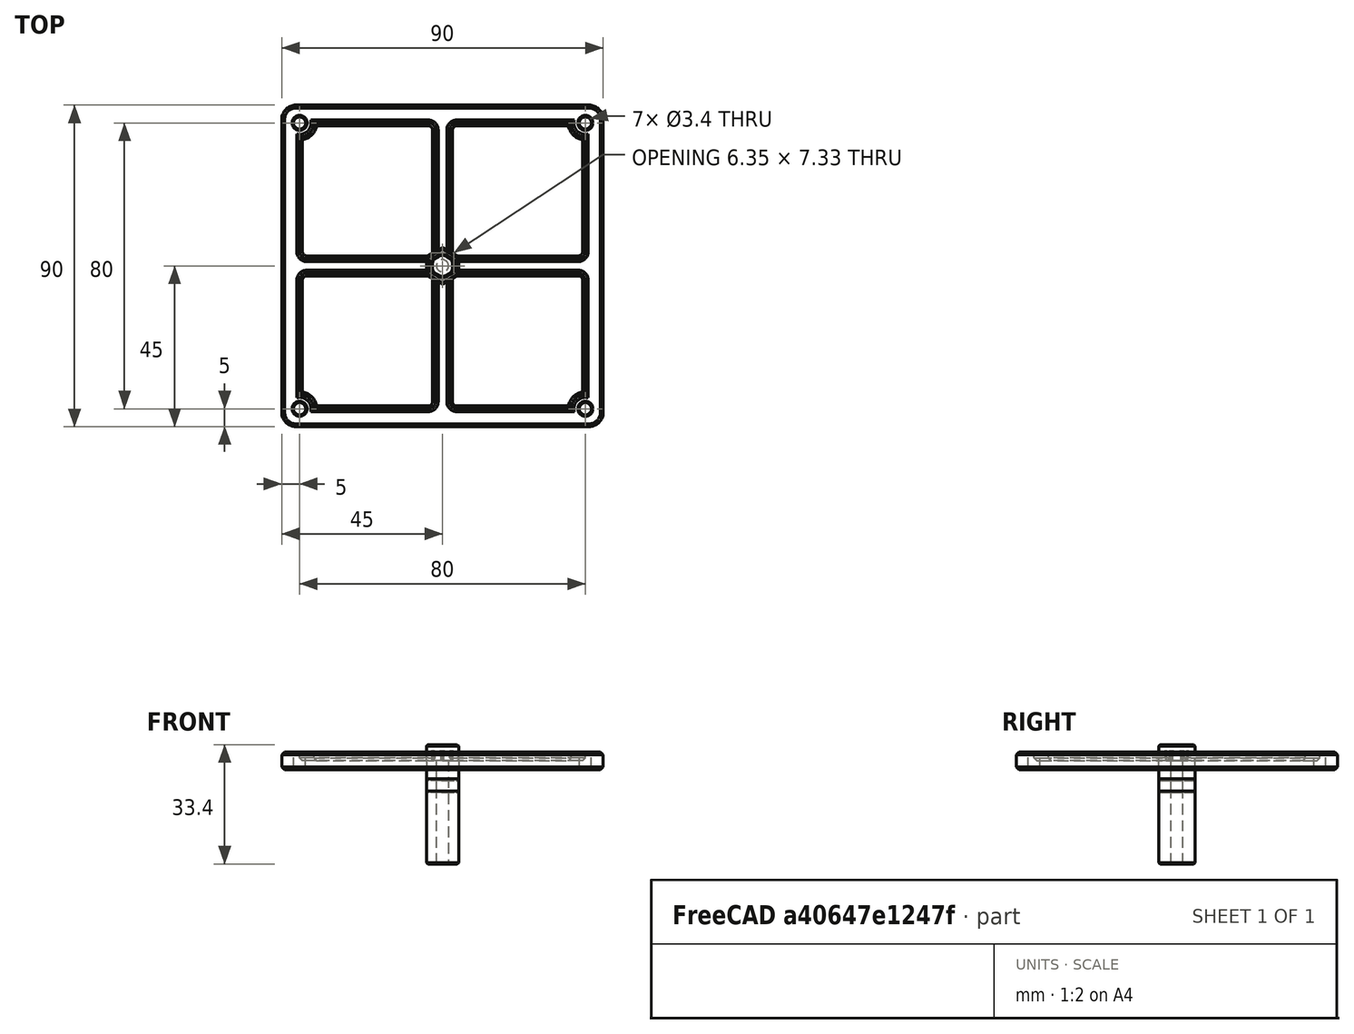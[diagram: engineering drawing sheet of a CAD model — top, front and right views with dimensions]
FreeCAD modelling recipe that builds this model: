
FCSTD DOCUMENT  (FreeCAD 1.1R20260325 (Git shallow))
Label: test_jig
License: All rights reserved
LicenseURL: http://en.wikipedia.org/wiki/All_rights_reserved
objects: Sketcher::SketchObject×9, PartDesign::Chamfer×8, PartDesign::Body×5, App::Point×5, PartDesign::Pad×4, PartDesign::Pocket×3, PartDesign::FeatureBase×3, PartDesign::Fillet×1, PartDesign::AdditiveLoft×1
note: 80 computed .brp shape members not serialized (recipe doc carries the construction recipe); baked Part::Feature solids carry a one-line shape summary decoded from their .brp

FEATURE [Sketcher::SketchObject] Sketch  label="dc_base_s"
  ArcFitTolerance = 1e-06
  AttachmentSupport = -> [XY_Plane]
  ExternalTypes = [0]
  FullyConstrained = true
  MakeInternals = false
  MapMode = 5
  _ExternalGeoVersion = 0
  sketch-geometry (4):
    g0: LineSegment StartX=-45 StartY=45 StartZ=0 EndX=-45 EndY=-45 EndZ=0
    g1: LineSegment StartX=-45 StartY=-45 StartZ=0 EndX=45 EndY=-45 EndZ=0
    g2: LineSegment StartX=45 StartY=-45 StartZ=0 EndX=45 EndY=45 EndZ=0
    g3: LineSegment StartX=45 StartY=45 StartZ=0 EndX=-45 EndY=45 EndZ=0
  constraints (10):
    c: Coincident(g0,g1)
    c: Coincident(g1,g2)
    c: Coincident(g2,g3)
    c: Coincident(g3,g0)
    c: Vertical(g2)
    c: Horizontal(g1)
    c: Symmetric(g0,g0,g-1)
    c: Symmetric(g0,g2,g-2)
    c: DistanceX(g1,g1) = 90  'dim2'
    c: DistanceY(g0,g0) = 90  'dim1'
FEATURE [PartDesign::Pad] Pad  label="dc_base"
  Direction = (0,0,1)
  Length = 5
  Length2 = 10
  Profile = -> Sketch
  ReferenceAxis = -> Sketch [N_Axis]
  Refine = true
  SideType = 2
  Suppressed = false
  Type = 0
  Type2 = 0
FEATURE [Sketcher::SketchObject] Sketch001  label="dc_grid_cut_s"
  ArcFitTolerance = 1e-06
  AttachmentSupport = -> [XY_Plane]
  ExternalTypes = [0]
  FullyConstrained = false
  MakeInternals = false
  MapMode = 5
  _ExternalGeoVersion = 0
  expr: .Constraints.corner_flt = <<dc_base_corner>>.Radius
  expr: .Constraints.dim1 = <<dc_base_s>>.Constraints.dim1
  expr: .Constraints.dim2 = <<dc_base_s>>.Constraints.dim2
  sketch-geometry (76):
    g0: LineSegment StartX=-40 StartY=36 StartZ=0 EndX=-40 EndY=4 EndZ=0
    g1: LineSegment StartX=-38 StartY=2 StartZ=0 EndX=-4 EndY=2 EndZ=0
    g2: LineSegment StartX=-2 StartY=4 StartZ=0 EndX=-2 EndY=38 EndZ=0
    g3: LineSegment StartX=-4 StartY=40 StartZ=0 EndX=-36 EndY=40 EndZ=0
    g4: LineSegment StartX=2 StartY=38 StartZ=0 EndX=2 EndY=4 EndZ=0
    g5: LineSegment StartX=4 StartY=2 StartZ=0 EndX=38 EndY=2 EndZ=0
    g6: LineSegment StartX=40 StartY=4 StartZ=0 EndX=40 EndY=36 EndZ=0
    g7: LineSegment StartX=36 StartY=40 StartZ=0 EndX=4 EndY=40 EndZ=0
    g8: LineSegment StartX=-40 StartY=-4 StartZ=0 EndX=-40 EndY=-36 EndZ=0
    g9: LineSegment StartX=-2 StartY=-38 StartZ=0 EndX=-2 EndY=-4 EndZ=0
    g10: LineSegment StartX=-4 StartY=-2 StartZ=0 EndX=-38 EndY=-2 EndZ=0
    g11: LineSegment StartX=2 StartY=-4 StartZ=0 EndX=2 EndY=-38 EndZ=0
    g12: LineSegment StartX=4 StartY=-40 StartZ=0 EndX=36 EndY=-40 EndZ=0
    g13: LineSegment StartX=40 StartY=-36 StartZ=0 EndX=40 EndY=-4 EndZ=0
    g14: LineSegment StartX=38 StartY=-2 StartZ=0 EndX=4 EndY=-2 EndZ=0
    g15: LineSegment [constr] StartX=-45 StartY=45 StartZ=0 EndX=-45 EndY=-45 EndZ=0
    g16: LineSegment [constr] StartX=-45 StartY=-45 StartZ=0 EndX=45 EndY=-45 EndZ=0
    g17: LineSegment [constr] StartX=45 StartY=-45 StartZ=0 EndX=45 EndY=45 EndZ=0
    g18: LineSegment [constr] StartX=45 StartY=45 StartZ=0 EndX=-45 EndY=45 EndZ=0
    g19: GeomPoint [constr] X=-40 Y=40 Z=0
    g20: ArcOfCircle CenterX=-4 CenterY=38 CenterZ=0 NormalX=0 NormalY=0 NormalZ=1 AngleXU=0 Radius=2 StartAngle=1.6e-15 EndAngle=1.5708
    g21: GeomPoint [constr] X=-2 Y=40 Z=0
    g22: ArcOfCircle CenterX=-4 CenterY=4 CenterZ=0 NormalX=0 NormalY=0 NormalZ=1 AngleXU=0 Radius=2 StartAngle=4.71239 EndAngle=6.28319
    g23: GeomPoint [constr] X=-2 Y=2 Z=0
    g24: ArcOfCircle CenterX=-38 CenterY=4 CenterZ=0 NormalX=0 NormalY=0 NormalZ=1 AngleXU=0 Radius=2 StartAngle=3.14159 EndAngle=4.71239
    g25: GeomPoint [constr] X=-40 Y=2 Z=0
    g26: ArcOfCircle CenterX=-38 CenterY=-4 CenterZ=0 NormalX=0 NormalY=0 NormalZ=1 AngleXU=0 Radius=2 StartAngle=1.5708 EndAngle=3.14159
    g27: GeomPoint [constr] X=-40 Y=-2 Z=0
    g28: GeomPoint [constr] X=-35 Y=-35 Z=0
    g29: ArcOfCircle CenterX=-4 CenterY=-38 CenterZ=0 NormalX=0 NormalY=0 NormalZ=1 AngleXU=0 Radius=2 StartAngle=4.71239 EndAngle=6.28319
    g30: GeomPoint [constr] X=-2 Y=-35 Z=0
    g31: ArcOfCircle CenterX=-4 CenterY=-4 CenterZ=0 NormalX=0 NormalY=0 NormalZ=1 AngleXU=0 Radius=2 StartAngle=1e-16 EndAngle=1.5708
    g32: GeomPoint [constr] X=-2 Y=-2 Z=0
    g33: ArcOfCircle CenterX=4 CenterY=38 CenterZ=0 NormalX=0 NormalY=0 NormalZ=1 AngleXU=0 Radius=2 StartAngle=1.5708 EndAngle=3.14159
    g34: GeomPoint [constr] X=2 Y=40 Z=0
    g35: GeomPoint [constr] X=40 Y=40 Z=0
    g36: ArcOfCircle CenterX=38 CenterY=-4 CenterZ=0 NormalX=0 NormalY=0 NormalZ=1 AngleXU=0 Radius=2 StartAngle=0 EndAngle=1.5708
    g37: GeomPoint [constr] X=40 Y=-2 Z=0
    g38: ArcOfCircle CenterX=4 CenterY=-4 CenterZ=0 NormalX=0 NormalY=0 NormalZ=1 AngleXU=0 Radius=2 StartAngle=1.5708 EndAngle=3.14159
    g39: GeomPoint [constr] X=2 Y=-2 Z=0
    g40: ArcOfCircle CenterX=4 CenterY=-38 CenterZ=0 NormalX=0 NormalY=0 NormalZ=1 AngleXU=0 Radius=2 StartAngle=3.14159 EndAngle=4.71239
    g41: GeomPoint [constr] X=2 Y=-40 Z=0
    g42: GeomPoint [constr] X=40 Y=-40 Z=0
    g43: ArcOfCircle CenterX=4 CenterY=4 CenterZ=0 NormalX=0 NormalY=0 NormalZ=1 AngleXU=0 Radius=2 StartAngle=3.14159 EndAngle=4.71239
    g44: GeomPoint [constr] X=2 Y=2 Z=0
    g45: ArcOfCircle CenterX=38 CenterY=4 CenterZ=0 NormalX=0 NormalY=0 NormalZ=1 AngleXU=0 Radius=2 StartAngle=4.71239 EndAngle=6.28319
    g46: GeomPoint [constr] X=40 Y=2 Z=0
    g47: LineSegment [constr] StartX=-4 StartY=2 StartZ=0 EndX=-4 EndY=-2 EndZ=0
    g48: LineSegment [constr] StartX=4 StartY=2 StartZ=0 EndX=4 EndY=-2 EndZ=0
    g49: LineSegment [constr] StartX=-2 StartY=4 StartZ=0 EndX=2 EndY=4 EndZ=0
    g50: LineSegment [constr] StartX=-2 StartY=-4 StartZ=0 EndX=2 EndY=-4 EndZ=0
    g51: Circle [constr] CenterX=0 CenterY=0 CenterZ=0 NormalX=0 NormalY=0 NormalZ=1 AngleXU=0 Radius=4
    g52: LineSegment [constr] StartX=-40 StartY=4 StartZ=0 EndX=-45 EndY=4 EndZ=0
    g53: LineSegment [constr] StartX=-40 StartY=-4 StartZ=0 EndX=-45 EndY=-4 EndZ=0
    g54: LineSegment [constr] StartX=40 StartY=4 StartZ=0 EndX=45 EndY=4 EndZ=0
    g55: LineSegment [constr] StartX=40 StartY=-4 StartZ=0 EndX=45 EndY=-4 EndZ=0
    g56: LineSegment [constr] StartX=4 StartY=-40 StartZ=0 EndX=4 EndY=-45 EndZ=0
    g57: LineSegment [constr] StartX=-4 StartY=-40 StartZ=0 EndX=-4 EndY=-45 EndZ=0
    g58: LineSegment [constr] StartX=-4 StartY=40 StartZ=0 EndX=-4 EndY=45 EndZ=0
    g59: LineSegment [constr] StartX=4 StartY=40 StartZ=0 EndX=4 EndY=45 EndZ=0
    g60: LineSegment [constr] StartX=-45 StartY=-40 StartZ=0 EndX=-40 EndY=-40 EndZ=0
    g61: LineSegment [constr] StartX=-40 StartY=-40 StartZ=0 EndX=-40 EndY=-45 EndZ=0
    g62: Circle [constr] CenterX=-40 CenterY=-40 CenterZ=0 NormalX=0 NormalY=0 NormalZ=1 AngleXU=0 Radius=1.7
    g63: Circle [constr] CenterX=-40 CenterY=-40 CenterZ=0 NormalX=0 NormalY=0 NormalZ=1 AngleXU=0 Radius=2.8
    g64: ArcOfCircle CenterX=-40 CenterY=-40 CenterZ=0 NormalX=0 NormalY=0 NormalZ=1 AngleXU=0 Radius=4 StartAngle=-9e-16 EndAngle=1.5708
    g65: ArcOfCircle [constr] CenterX=-41 CenterY=-41 CenterZ=0 NormalX=0 NormalY=0 NormalZ=1 AngleXU=0 Radius=4 StartAngle=3.14159 EndAngle=4.71239
    g66: LineSegment [constr] StartX=40 StartY=-45 StartZ=0 EndX=40 EndY=-40 EndZ=0
    g67: LineSegment [constr] StartX=40 StartY=-40 StartZ=0 EndX=45 EndY=-40 EndZ=0
    g68: LineSegment [constr] StartX=40 StartY=45 StartZ=0 EndX=40 EndY=40 EndZ=0
    g69: LineSegment [constr] StartX=40 StartY=40 StartZ=0 EndX=45 EndY=40 EndZ=0
    g70: LineSegment [constr] StartX=-45 StartY=40 StartZ=0 EndX=-40 EndY=40 EndZ=0
    g71: LineSegment [constr] StartX=-40 StartY=40 StartZ=0 EndX=-40 EndY=45 EndZ=0
    g72: ArcOfCircle CenterX=40 CenterY=-40 CenterZ=0 NormalX=0 NormalY=0 NormalZ=1 AngleXU=0 Radius=4 StartAngle=1.5708 EndAngle=3.14159
    g73: ArcOfCircle CenterX=40 CenterY=40 CenterZ=0 NormalX=0 NormalY=0 NormalZ=1 AngleXU=0 Radius=4 StartAngle=3.14159 EndAngle=4.71239
    g74: ArcOfCircle CenterX=-40 CenterY=40 CenterZ=0 NormalX=0 NormalY=0 NormalZ=1 AngleXU=0 Radius=4 StartAngle=4.71239 EndAngle=6.28319
    g75: LineSegment StartX=-36 StartY=-40 StartZ=0 EndX=-4 EndY=-40 EndZ=0
  constraints (192):
    c: Vertical(g0)
    c: Vertical(g2)
    c: Horizontal(g1)
    c: Horizontal(g3)
    c: Vertical(g4)
    c: Vertical(g6)
    c: Horizontal(g5)
    c: Horizontal(g7)
    c: Vertical(g8)
    c: Vertical(g9)
    c: Horizontal(g10)
    c: Vertical(g11)
    c: Vertical(g13)
    c: Horizontal(g12)
    c: Horizontal(g14)
    c: Coincident(g15,g16)
    c: Coincident(g16,g17)
    c: Coincident(g17,g18)
    c: Coincident(g18,g15)
    c: Vertical(g17)
    c: Horizontal(g16)
    c: Symmetric(g15,g17,g-2)
    c: Symmetric(g15,g15,g-1)
    c: DistanceX(g16,g16) = 90  'dim2'
    c: DistanceY(g15,g15) = 90  'dim1'
    c: PointOnObject(g19,g0)
    c: PointOnObject(g19,g3)
    c: PointOnObject(g21,g3)
    c: PointOnObject(g21,g2)
    c: Tangent(g3,g20) = -1.5708
    c: Tangent(g2,g20) = -1.5708
    c: PointOnObject(g23,g2)
    c: PointOnObject(g23,g1)
    c: Tangent(g2,g22) = -1.5708
    c: Tangent(g1,g22) = -1.5708
    c: PointOnObject(g25,g1)
    c: PointOnObject(g25,g0)
    c: Tangent(g1,g24) = -1.5708
    c: Tangent(g0,g24) = -1.5708
    c: PointOnObject(g27,g10)
    c: PointOnObject(g27,g8)
    c: Tangent(g10,g26) = -1.5708
    c: Tangent(g8,g26) = -1.5708
    c: PointOnObject(g30,g9)
    c: Tangent(g9,g29) = -1.5708
    c: PointOnObject(g32,g10)
    c: PointOnObject(g32,g9)
    c: Tangent(g10,g31) = -1.5708
    c: Tangent(g9,g31) = -1.5708
    c: PointOnObject(g34,g7)
    c: PointOnObject(g34,g4)
    c: Tangent(g7,g33) = -1.5708
    c: Tangent(g4,g33) = -1.5708
    c: PointOnObject(g35,g7)
    c: PointOnObject(g35,g6)
    c: PointOnObject(g37,g14)
    c: PointOnObject(g37,g13)
    c: Tangent(g14,g36) = -1.5708
    c: Tangent(g13,g36) = -1.5708
    c: PointOnObject(g39,g14)
    c: PointOnObject(g39,g11)
    c: Tangent(g14,g38) = -1.5708
    c: Tangent(g11,g38) = -1.5708
    c: PointOnObject(g41,g11)
    c: PointOnObject(g41,g12)
    c: Tangent(g11,g40) = -1.5708
    c: Tangent(g12,g40) = -1.5708
    c: PointOnObject(g42,g12)
    c: PointOnObject(g42,g13)
    c: PointOnObject(g44,g4)
    c: PointOnObject(g44,g5)
    c: Tangent(g4,g43) = -1.5708
    c: Tangent(g5,g43) = -1.5708
    c: PointOnObject(g46,g5)
    c: PointOnObject(g46,g6)
    c: Tangent(g5,g45) = -1.5708
    c: Tangent(g6,g45) = -1.5708
    c: Coincident(g47,g1)
    c: Coincident(g47,g10)
    c: Vertical(g47)
    c: Coincident(g48,g5)
    c: Coincident(g48,g14)
    c: Coincident(g49,g2)
    c: Coincident(g49,g4)
    c: Coincident(g50,g9)
    c: Coincident(g50,g11)
    c: Horizontal(g49)
    c: Horizontal(g50)
    c: Vertical(g48)
    c: DistanceY(g47,g47) = 4  'rim_inner'
    c: Coincident(g51,g-1)
    c: Tangent(g49,g51)
    c: Tangent(g48,g51)
    c: Tangent(g50,g51)
    c: Tangent(g51,g47)
    c: Coincident(g52,g0)
    c: PointOnObject(g52,g15)
    c: Horizontal(g52)
    c: Coincident(g53,g8)
    c: PointOnObject(g53,g15)
    c: Horizontal(g53)
    c: Coincident(g54,g6)
    c: PointOnObject(g54,g17)
    c: Coincident(g55,g13)
    c: PointOnObject(g55,g17)
    c: Coincident(g56,g12)
    c: PointOnObject(g56,g16)
    c: PointOnObject(g57,g16)
    c: Coincident(g58,g3)
    c: PointOnObject(g58,g18)
    c: Coincident(g59,g7)
    c: PointOnObject(g59,g18)
    c: Vertical(g57)
    c: Vertical(g56)
    c: Vertical(g58)
    c: Vertical(g59)
    c: Horizontal(g54)
    c: Horizontal(g55)
    c: Equal(g52,g53)
    c: Equal(g53,g57)
    c: Equal(g57,g56)
    c: Equal(g56,g55)
    c: Equal(g55,g54)
    c: Equal(g54,g59)
    c: Equal(g59,g58)
    c: Distance(g52,g52) = 5  'rib_outer'
    c: PointOnObject(g60,g15)
    c: Horizontal(g60)
    c: Coincident(g60,g61)
    c: PointOnObject(g61,g16)
    c: Vertical(g61)
    c: Coincident(g62,g60)
    c: Coincident(g63,g60)
    c: Diameter(g62) = 3.4  'screw_hole'
    c: Diameter(g63) = 5.6  'screw_head'
    c: Coincident(g64,g60)
    c: DistanceX(g60,g60) = 5  'screw_inset'
    c: Equal(g61,g60)
    c: Tangent(g65,g15) = -1.5708
    c: Tangent(g65,g16) = -1.5708
    c: Radius(g65) = 4  'corner_flt'
    c: PointOnObject(g66,g16)
    c: Vertical(g66)
    c: Coincident(g66,g67)
    c: PointOnObject(g67,g17)
    c: Horizontal(g67)
    c: PointOnObject(g68,g18)
    c: Vertical(g68)
    c: Coincident(g68,g69)
    c: PointOnObject(g69,g17)
    c: Horizontal(g69)
    c: PointOnObject(g70,g15)
    c: Coincident(g70,g71)
    c: PointOnObject(g71,g18)
    c: Radius(g20) = 2  'corner_fillet'
    c: Horizontal(g70)
    c: Vertical(g71)
    c: Equal(g61,g66)
    c: Equal(g66,g67)
    c: Equal(g67,g69)
    c: Equal(g69,g68)
    c: Equal(g68,g71)
    c: Equal(g71,g70)
    c: Coincident(g72,g42)
    c: Coincident(g73,g35)
    c: Coincident(g74,g19)
    c: Coincident(g3,g74)
    c: Coincident(g0,g74)
    c: Coincident(g7,g73)
    c: Coincident(g6,g73)
    c: Coincident(g13,g72)
    c: Coincident(g12,g72)
    c: Coincident(g8,g64)
    c: Equal(g20,g33)
    c: Equal(g33,g45)
    c: Equal(g45,g36)
    c: Equal(g36,g40)
    c: Equal(g40,g29)
    c: Equal(g29,g26)
    c: Equal(g26,g24)
    c: Equal(g24,g43)
    c: Equal(g43,g38)
    c: Equal(g38,g31)
    c: Equal(g31,g22)
    c: Coincident(g75,g64)
    c: Horizontal(g75)
    c: Tangent(g29,g75) = -1.5708
    c: Coincident(g57,g29)
    c: Equal(g72,g64)
    c: Equal(g64,g74)
    c: Equal(g74,g73)
    c: Radius(g64) = 4  'screw_pad'
FEATURE [PartDesign::Fillet] Fillet  label="dc_base_corner"
  Base = -> Pad [Edge2,Edge5,Edge8,Edge1]
  BaseFeature = -> Pad
  Radius = 4
  Refine = true
  SupportTransform = false
  Suppressed = false
  UseAllEdges = false
FEATURE [PartDesign::Pocket] Pocket  label="dc_grid_cut"
  BaseFeature = -> Fillet
  Direction = (0,0,-1)
  Length = 5
  Length2 = 5
  Profile = -> Sketch001
  ReferenceAxis = -> Sketch001 [N_Axis]
  Refine = true
  Reversed = true
  SideType = 0
  Suppressed = false
  Type = 1
  Type2 = 0
FEATURE [Sketcher::SketchObject] Sketch002  label="dc_holes_s"
  ArcFitTolerance = 1e-06
  AttachmentSupport = -> [XY_Plane]
  ExternalTypes = [0]
  FullyConstrained = true
  MakeInternals = false
  MapMode = 5
  _ExternalGeoVersion = 0
  expr: .Constraints.dim1 = <<dc_base_s>>.Constraints.dim1
  expr: .Constraints.dim2 = <<dc_base_s>>.Constraints.dim2
  expr: .Constraints.head = <<dc_grid_cut_s>>.Constraints.screw_head
  expr: .Constraints.hole = <<dc_grid_cut_s>>.Constraints.screw_hole
  expr: .Constraints.inset = <<dc_grid_cut_s>>.Constraints.screw_inset
  sketch-geometry (17):
    g0: LineSegment [constr] StartX=-45 StartY=45 StartZ=0 EndX=-45 EndY=-45 EndZ=0
    g1: LineSegment [constr] StartX=-45 StartY=-45 StartZ=0 EndX=45 EndY=-45 EndZ=0
    g2: LineSegment [constr] StartX=45 StartY=-45 StartZ=0 EndX=45 EndY=45 EndZ=0
    g3: LineSegment [constr] StartX=45 StartY=45 StartZ=0 EndX=-45 EndY=45 EndZ=0
    g4: LineSegment [constr] StartX=-40 StartY=45 StartZ=0 EndX=-40 EndY=40 EndZ=0
    g5: LineSegment [constr] StartX=-40 StartY=40 StartZ=0 EndX=-45 EndY=40 EndZ=0
    g6: LineSegment [constr] StartX=40 StartY=45 StartZ=0 EndX=40 EndY=40 EndZ=0
    g7: LineSegment [constr] StartX=40 StartY=40 StartZ=0 EndX=45 EndY=40 EndZ=0
    g8: LineSegment [constr] StartX=-45 StartY=-40 StartZ=0 EndX=-40 EndY=-40 EndZ=0
    g9: LineSegment [constr] StartX=-40 StartY=-40 StartZ=0 EndX=-40 EndY=-45 EndZ=0
    g10: LineSegment [constr] StartX=45 StartY=-40 StartZ=0 EndX=40 EndY=-40 EndZ=0
    g11: LineSegment [constr] StartX=40 StartY=-40 StartZ=0 EndX=40 EndY=-45 EndZ=0
    g12: Circle CenterX=-40 CenterY=-40 CenterZ=0 NormalX=0 NormalY=0 NormalZ=1 AngleXU=0 Radius=1.7
    g13: Circle CenterX=40 CenterY=-40 CenterZ=0 NormalX=0 NormalY=0 NormalZ=1 AngleXU=0 Radius=1.7
    g14: Circle CenterX=40 CenterY=40 CenterZ=0 NormalX=0 NormalY=0 NormalZ=1 AngleXU=0 Radius=1.7
    g15: Circle CenterX=-40 CenterY=40 CenterZ=0 NormalX=0 NormalY=0 NormalZ=1 AngleXU=0 Radius=1.7
    g16: Circle [constr] CenterX=-40 CenterY=-40 CenterZ=0 NormalX=0 NormalY=0 NormalZ=1 AngleXU=0 Radius=2.8
  constraints (48):
    c: Coincident(g0,g1)
    c: Coincident(g1,g2)
    c: Coincident(g2,g3)
    c: Coincident(g3,g0)
    c: Vertical(g2)
    c: Horizontal(g3)
    c: Symmetric(g0,g0,g-1)
    c: Symmetric(g0,g1,g-2)
    c: DistanceY(g0,g0) = 90  'dim1'
    c: DistanceX(g1,g1) = 90  'dim2'
    c: Vertical(g4)
    c: Coincident(g4,g5)
    c: Horizontal(g5)
    c: Vertical(g6)
    c: Coincident(g6,g7)
    c: Horizontal(g7)
    c: Horizontal(g8)
    c: Coincident(g8,g9)
    c: Vertical(g9)
    c: Horizontal(g10)
    c: Coincident(g10,g11)
    c: Vertical(g11)
    c: PointOnObject(g5,g0)
    c: PointOnObject(g8,g0)
    c: PointOnObject(g9,g1)
    c: PointOnObject(g11,g1)
    c: PointOnObject(g10,g2)
    c: PointOnObject(g7,g2)
    c: PointOnObject(g6,g3)
    c: PointOnObject(g4,g3)
    c: Equal(g5,g4)
    c: Equal(g4,g6)
    c: Equal(g6,g7)
    c: Equal(g7,g10)
    c: Equal(g10,g11)
    c: Equal(g11,g9)
    c: Equal(g9,g8)
    c: Distance(g8,g8) = 5  'inset'
    c: Coincident(g12,g8)
    c: Coincident(g13,g10)
    c: Coincident(g14,g6)
    c: Coincident(g15,g4)
    c: Diameter(g12) = 3.4  'hole'
    c: Equal(g13,g12)
    c: Equal(g12,g14)
    c: Equal(g14,g15)
    c: Coincident(g16,g8)
    c: Diameter(g16) = 5.6  'head'
FEATURE [PartDesign::Chamfer] Chamfer  label="dc_grid_chmf"
  Angle = 45
  Base = -> Pocket [Face43,Face45,Face46,Face44]
  BaseFeature = -> Pocket
  ChamferType = 0
  FlipDirection = false
  Refine = true
  Size = 0.8
  Size2 = 1
  SupportTransform = false
  Suppressed = false
  UseAllEdges = false
FEATURE [PartDesign::Chamfer] Chamfer001  label="dc_face_chmf"
  Angle = 45
  Base = -> Chamfer [Face51,Face4]
  BaseFeature = -> Chamfer
  ChamferType = 0
  FlipDirection = false
  Refine = true
  Size = 0.8
  Size2 = 1
  SupportTransform = false
  Suppressed = false
  UseAllEdges = false
FEATURE [PartDesign::Pocket] Pocket001  label="dc_holes"
  BaseFeature = -> Chamfer001
  Direction = (0,0,-1)
  Length = 5
  Length2 = 5
  Profile = -> Sketch002
  ReferenceAxis = -> Sketch002 [N_Axis]
  Refine = true
  SideType = 2
  Suppressed = false
  Type = 1
  Type2 = 0
FEATURE [PartDesign::Chamfer] Chamfer002  label="dc_holes_chmf"
  Angle = 45
  Base = -> Pocket001 [Edge56,Edge65,Edge39,Edge32,Edge99,Edge106,Edge158,Edge140]
  BaseFeature = -> Pocket001
  ChamferType = 0
  FlipDirection = false
  Refine = true
  Size = 0.4
  Size2 = 1
  SupportTransform = false
  Suppressed = false
  UseAllEdges = false
FEATURE [PartDesign::Body] Body  label="duct_cover"
  AllowCompound = false
  Group = -> [Sketch,Pad,Sketch001,Fillet,Pocket,Sketch002,Chamfer,Chamfer001,Pocket001,Chamfer002]
  Origin = -> Origin
  Tip = -> Chamfer002
FEATURE [Sketcher::SketchObject] Sketch007  label="spc_end_base_s"
  ArcFitTolerance = 1e-06
  AttachmentSupport = -> [XY_Plane003]
  ExternalTypes = [0]
  FullyConstrained = true
  MakeInternals = false
  MapMode = 5
  _ExternalGeoVersion = 0
  sketch-geometry (43):
    g0: LineSegment StartX=-3e-16 StartY=3.08882 StartZ=0 EndX=-2.675 EndY=1.54441 EndZ=0
    g1: LineSegment StartX=-2.675 StartY=1.54441 StartZ=0 EndX=-2.675 EndY=-1.54441 EndZ=0
    g2: LineSegment StartX=-2.675 StartY=-1.54441 StartZ=0 EndX=0 EndY=-3.08882 EndZ=0
    g3: LineSegment StartX=-2e-16 StartY=-3.08882 StartZ=0 EndX=2.675 EndY=-1.54441 EndZ=0
    g4: LineSegment StartX=2.675 StartY=-1.54441 StartZ=0 EndX=2.675 EndY=1.54441 EndZ=0
    g5: LineSegment StartX=2.675 StartY=1.54441 StartZ=0 EndX=-4e-16 EndY=3.08882 EndZ=0
    g6: Circle [constr] CenterX=0 CenterY=0 CenterZ=0 NormalX=0 NormalY=0 NormalZ=1 AngleXU=0 Radius=3.08882
    g7: LineSegment StartX=-4.5 StartY=2.02073 StartZ=0 EndX=-4.5 EndY=-2.02073 EndZ=0
    g8: LineSegment StartX=-4 StartY=-2.88675 StartZ=0 EndX=-0.5 EndY=-4.90748 EndZ=0
    g9: LineSegment StartX=0.5 StartY=-4.90748 StartZ=0 EndX=4 EndY=-2.88675 EndZ=0
    g10: LineSegment StartX=4.5 StartY=-2.02073 StartZ=0 EndX=4.5 EndY=2.02073 EndZ=0
    g11: LineSegment StartX=4 StartY=2.88675 StartZ=0 EndX=0.5 EndY=4.90748 EndZ=0
    g12: LineSegment StartX=-0.5 StartY=4.90748 StartZ=0 EndX=-4 EndY=2.88675 EndZ=0
    g13: Circle [constr] CenterX=0 CenterY=0 CenterZ=0 NormalX=0 NormalY=0 NormalZ=1 AngleXU=0 Radius=5.19615
    g14: ArcOfCircle CenterX=-3.5 CenterY=2.02073 CenterZ=0 NormalX=0 NormalY=0 NormalZ=1 AngleXU=0 Radius=1 StartAngle=2.0944 EndAngle=3.14159
    g15: GeomPoint [constr] X=-4.5 Y=2.59808 Z=0
    g16: ArcOfCircle CenterX=-3e-16 CenterY=4.04145 CenterZ=0 NormalX=0 NormalY=0 NormalZ=1 AngleXU=0 Radius=1 StartAngle=1.0472 EndAngle=2.0944
    g17: GeomPoint [constr] X=-5e-16 Y=5.19615 Z=0
    g18: ArcOfCircle CenterX=3.5 CenterY=2.02073 CenterZ=0 NormalX=0 NormalY=0 NormalZ=1 AngleXU=0 Radius=1 StartAngle=0 EndAngle=1.0472
    g19: GeomPoint [constr] X=4.5 Y=2.59808 Z=0
    g20: ArcOfCircle CenterX=3.5 CenterY=-2.02073 CenterZ=0 NormalX=0 NormalY=0 NormalZ=1 AngleXU=0 Radius=1 StartAngle=5.23599 EndAngle=6.28319
    g21: GeomPoint [constr] X=4.5 Y=-2.59808 Z=0
    g22: ArcOfCircle CenterX=1e-16 CenterY=-4.04145 CenterZ=0 NormalX=0 NormalY=0 NormalZ=1 AngleXU=0 Radius=1 StartAngle=4.18879 EndAngle=5.23599
    g23: GeomPoint [constr] X=1.8e-15 Y=-5.19615 Z=0
    g24: ArcOfCircle CenterX=-3.5 CenterY=-2.02073 CenterZ=0 NormalX=0 NormalY=0 NormalZ=1 AngleXU=0 Radius=1 StartAngle=3.14159 EndAngle=4.18879
    g25: GeomPoint [constr] X=-4.5 Y=-2.59808 Z=0
    g26: Circle [constr] CenterX=0 CenterY=0 CenterZ=0 NormalX=0 NormalY=0 NormalZ=1 AngleXU=0 Radius=1.7
    g27: LineSegment [constr] StartX=0 StartY=0 StartZ=0 EndX=0 EndY=-4.5 EndZ=0
    g28: LineSegment [constr] StartX=2.675 StartY=-1.54441 StartZ=0 EndX=4.5 EndY=-1.54441 EndZ=0
    g29: LineSegment [constr] StartX=-2.725 StartY=1.57328 StartZ=0 EndX=-2.725 EndY=-1.57328 EndZ=0
    g30: LineSegment [constr] StartX=-2.725 StartY=-1.57328 StartZ=0 EndX=0 EndY=-3.14656 EndZ=0
    g31: LineSegment [constr] StartX=0 StartY=-3.14656 StartZ=0 EndX=2.725 EndY=-1.57328 EndZ=0
    g32: LineSegment [constr] StartX=2.725 StartY=-1.57328 StartZ=0 EndX=2.725 EndY=1.57328 EndZ=0
    g33: LineSegment [constr] StartX=2.725 StartY=1.57328 StartZ=0 EndX=0 EndY=3.14656 EndZ=0
    g34: LineSegment [constr] StartX=0 StartY=3.14656 StartZ=0 EndX=-2.725 EndY=1.57328 EndZ=0
    g35: Circle [constr] CenterX=0 CenterY=0 CenterZ=0 NormalX=0 NormalY=0 NormalZ=1 AngleXU=0 Radius=3.14656
    g36: LineSegment [constr] StartX=-2.775 StartY=1.60215 StartZ=0 EndX=-2.775 EndY=-1.60215 EndZ=0
    g37: LineSegment [constr] StartX=-2.775 StartY=-1.60215 StartZ=0 EndX=0 EndY=-3.20429 EndZ=0
    g38: LineSegment [constr] StartX=1e-16 StartY=-3.20429 StartZ=0 EndX=2.775 EndY=-1.60215 EndZ=0
    g39: LineSegment [constr] StartX=2.775 StartY=-1.60215 StartZ=0 EndX=2.775 EndY=1.60215 EndZ=0
    g40: LineSegment [constr] StartX=2.775 StartY=1.60215 StartZ=0 EndX=0 EndY=3.20429 EndZ=0
    g41: LineSegment [constr] StartX=-1e-16 StartY=3.20429 StartZ=0 EndX=-2.775 EndY=1.60215 EndZ=0
    g42: Circle [constr] CenterX=0 CenterY=0 CenterZ=0 NormalX=0 NormalY=0 NormalZ=1 AngleXU=0 Radius=3.20429
  constraints (102):
    c: Coincident(g0,g1)
    c: Coincident(g1,g2)
    c: Coincident(g2,g3)
    c: Coincident(g3,g4)
    c: Coincident(g4,g5)
    c: Coincident(g5,g0)
    c: Equal(g0, g1-g5) x5
    c: PointOnObject(g0,g6)
    c: PointOnObject(g1,g6)
    c: PointOnObject(g2,g6)
    c: PointOnObject(g3,g6)
    c: PointOnObject(g4,g6)
    c: PointOnObject(g5,g6)
    c: Coincident(g6,g-1)
    c: PointOnObject(g25,g13)
    c: PointOnObject(g23,g13)
    c: PointOnObject(g21,g13)
    c: PointOnObject(g19,g13)
    c: PointOnObject(g17,g13)
    c: PointOnObject(g15,g13)
    c: Coincident(g13,g6)
    c: PointOnObject(g15,g7)
    c: PointOnObject(g15,g12)
    c: Tangent(g7,g14) = -1.5708
    c: Tangent(g12,g14) = -1.5708
    c: PointOnObject(g17,g12)
    c: PointOnObject(g17,g11)
    c: Tangent(g12,g16) = -1.5708
    c: Tangent(g11,g16) = -1.5708
    c: PointOnObject(g19,g11)
    c: PointOnObject(g19,g10)
    c: Tangent(g11,g18) = -1.5708
    c: Tangent(g10,g18) = -1.5708
    c: PointOnObject(g21,g10)
    c: PointOnObject(g21,g9)
    c: Tangent(g10,g20) = -1.5708
    c: Tangent(g9,g20) = -1.5708
    c: PointOnObject(g23,g8)
    c: PointOnObject(g23,g9)
    c: Tangent(g8,g22) = -1.5708
    c: Tangent(g9,g22) = -1.5708
    c: PointOnObject(g25,g7)
    c: PointOnObject(g25,g8)
    c: Tangent(g7,g24) = -1.5708
    c: Tangent(g8,g24) = -1.5708
    c: Equal(g8,g7)
    c: Equal(g7,g12)
    c: Equal(g12,g11)
    c: Equal(g11,g10)
    c: Equal(g10,g9)
    c: Equal(g16,g18)
    c: Equal(g18,g20)
    c: Equal(g20,g22)
    c: Equal(g22,g24)
    c: Equal(g24,g14)
    c: Distance(g7,g10) = 9  'outer_diam'
    c: Vertical(g7)
    c: Radius(g14) = 1  'outer_fillet'
    c: Vertical(g1)
    c: Coincident(g26,g6)
    c: Diameter(g26) = 3.4  'hole_diam'
    c: Coincident(g27,g6)
    c: PointOnObject(g27,g-2)
    c: DistanceY(g27,g27) = 4.5  'end_length'
    c: Distance(g3,g1) = 5.35  'nut_min_diam'
    c: Coincident(g3,g28)
    c: Perpendicular(g28,g10) = 1.5708
    c: DistanceX(g28,g28) = 1.825  'wall_thickness'
    c: Coincident(g29,g30)
    c: Coincident(g30,g31)
    c: Coincident(g31,g32)
    c: Coincident(g32,g33)
    c: Coincident(g33,g34)
    c: Coincident(g34,g29)
    c: Equal(g29, g30-g34) x5
    c: PointOnObject(g29,g35)
    c: PointOnObject(g30,g35)
    c: PointOnObject(g31,g35)
    c: PointOnObject(g32,g35)
    c: PointOnObject(g33,g35)
    c: PointOnObject(g34,g35)
    c: Coincident(g35,g6)
    c: Coincident(g36,g37)
    c: Coincident(g37,g38)
    c: Coincident(g38,g39)
    c: Coincident(g39,g40)
    c: Coincident(g40,g41)
    c: Coincident(g41,g36)
    c: Equal(g36, g37-g41) x5
    c: PointOnObject(g36,g42)
    c: PointOnObject(g37,g42)
    c: PointOnObject(g38,g42)
    c: PointOnObject(g39,g42)
    c: PointOnObject(g40,g42)
    c: PointOnObject(g41,g42)
    c: Coincident(g42,g6)
    c: Vertical(g29)
    c: Vertical(g36)
    c: Distance(g29,g32) = 5.45  'nut_diam'
    c: DistanceX(g36,g39) = 5.55  'nut_max_diam'
    c: DistanceX(g32,g39) = 0.05  'nut_max_offset'
    c: DistanceX(g3,g31) = 0.05  'nut_min_offset'
FEATURE [Sketcher::SketchObject] Sketch008  label="spc_end_end_s"
  ArcFitTolerance = 1e-06
  AttachmentOffset = pos=(0,0,4.5) rot=(0,0,1;0rad)
  AttachmentSupport = -> [XY_Plane003]
  ExternalTypes = [0]
  FullyConstrained = true
  MakeInternals = false
  MapMode = 5
  Placement = pos=(0,0,4.5) rot=(0,0,1;0rad)
  _ExternalGeoVersion = 0
  expr: .AttachmentOffset.Base.z = <<spc_end_base_s>>.Constraints.end_length
  expr: .Constraints.nut_max_diam = <<spc_end_base_s>>.Constraints.nut_max_diam
  expr: .Constraints.outer_diam = <<spc_end_base_s>>.Constraints.outer_diam
  expr: .Constraints.outer_fillet = <<spc_end_base_s>>.Constraints.outer_fillet
  sketch-geometry (27):
    g0: LineSegment StartX=-2.775 StartY=1.60215 StartZ=0 EndX=-2.775 EndY=-1.60215 EndZ=0
    g1: LineSegment StartX=-2.775 StartY=-1.60215 StartZ=0 EndX=0 EndY=-3.20429 EndZ=0
    g2: LineSegment StartX=1e-16 StartY=-3.20429 StartZ=0 EndX=2.775 EndY=-1.60215 EndZ=0
    g3: LineSegment StartX=2.775 StartY=-1.60215 StartZ=0 EndX=2.775 EndY=1.60215 EndZ=0
    g4: LineSegment StartX=2.775 StartY=1.60215 StartZ=0 EndX=0 EndY=3.20429 EndZ=0
    g5: LineSegment StartX=-1e-16 StartY=3.20429 StartZ=0 EndX=-2.775 EndY=1.60215 EndZ=0
    g6: Circle [constr] CenterX=0 CenterY=0 CenterZ=0 NormalX=0 NormalY=0 NormalZ=1 AngleXU=0 Radius=3.20429
    g7: LineSegment StartX=-4.5 StartY=2.02073 StartZ=0 EndX=-4.5 EndY=-2.02073 EndZ=0
    g8: LineSegment StartX=-4 StartY=-2.88675 StartZ=0 EndX=-0.5 EndY=-4.90748 EndZ=0
    g9: LineSegment StartX=0.5 StartY=-4.90748 StartZ=0 EndX=4 EndY=-2.88675 EndZ=0
    g10: LineSegment StartX=4.5 StartY=-2.02073 StartZ=0 EndX=4.5 EndY=2.02073 EndZ=0
    g11: LineSegment StartX=4 StartY=2.88675 StartZ=0 EndX=0.5 EndY=4.90748 EndZ=0
    g12: LineSegment StartX=-0.5 StartY=4.90748 StartZ=0 EndX=-4 EndY=2.88675 EndZ=0
    g13: Circle [constr] CenterX=0 CenterY=0 CenterZ=0 NormalX=0 NormalY=0 NormalZ=1 AngleXU=0 Radius=5.19615
    g14: ArcOfCircle CenterX=-3.5 CenterY=2.02073 CenterZ=0 NormalX=0 NormalY=0 NormalZ=1 AngleXU=0 Radius=1 StartAngle=2.0944 EndAngle=3.14159
    g15: GeomPoint [constr] X=-4.5 Y=2.59808 Z=0
    g16: ArcOfCircle CenterX=-3e-16 CenterY=4.04145 CenterZ=0 NormalX=0 NormalY=0 NormalZ=1 AngleXU=0 Radius=1 StartAngle=1.0472 EndAngle=2.0944
    g17: GeomPoint [constr] X=-9e-16 Y=5.19615 Z=0
    g18: ArcOfCircle CenterX=3.5 CenterY=2.02073 CenterZ=0 NormalX=0 NormalY=0 NormalZ=1 AngleXU=0 Radius=1 StartAngle=1e-16 EndAngle=1.0472
    g19: GeomPoint [constr] X=4.5 Y=2.59808 Z=0
    g20: ArcOfCircle CenterX=3.5 CenterY=-2.02073 CenterZ=0 NormalX=0 NormalY=0 NormalZ=1 AngleXU=0 Radius=1 StartAngle=5.23599 EndAngle=6.28319
    g21: GeomPoint [constr] X=4.5 Y=-2.59808 Z=0
    g22: ArcOfCircle CenterX=-1e-16 CenterY=-4.04145 CenterZ=0 NormalX=0 NormalY=0 NormalZ=1 AngleXU=0 Radius=1 StartAngle=4.18879 EndAngle=5.23599
    g23: GeomPoint [constr] X=9e-16 Y=-5.19615 Z=0
    g24: ArcOfCircle CenterX=-3.5 CenterY=-2.02073 CenterZ=0 NormalX=0 NormalY=0 NormalZ=1 AngleXU=0 Radius=1 StartAngle=3.14159 EndAngle=4.18879
    g25: GeomPoint [constr] X=-4.5 Y=-2.59808 Z=0
    g26: LineSegment [constr] StartX=1e-16 StartY=-3.20429 StartZ=0 EndX=-0.8625 EndY=-4.69819 EndZ=0
  constraints (63):
    c: Coincident(g0,g1)
    c: Coincident(g1,g2)
    c: Coincident(g2,g3)
    c: Coincident(g3,g4)
    c: Coincident(g4,g5)
    c: Coincident(g5,g0)
    c: Equal(g0, g1-g5) x5
    c: PointOnObject(g0,g6)
    c: PointOnObject(g1,g6)
    c: PointOnObject(g2,g6)
    c: PointOnObject(g3,g6)
    c: PointOnObject(g4,g6)
    c: PointOnObject(g5,g6)
    c: Coincident(g6,g-1)
    c: PointOnObject(g25,g13)
    c: PointOnObject(g23,g13)
    c: PointOnObject(g21,g13)
    c: PointOnObject(g19,g13)
    c: PointOnObject(g17,g13)
    c: PointOnObject(g15,g13)
    c: Coincident(g13,g6)
    c: PointOnObject(g15,g7)
    c: PointOnObject(g15,g12)
    c: Tangent(g7,g14) = -1.5708
    c: Tangent(g12,g14) = -1.5708
    c: PointOnObject(g17,g12)
    c: PointOnObject(g17,g11)
    c: Tangent(g12,g16) = -1.5708
    c: Tangent(g11,g16) = -1.5708
    c: PointOnObject(g19,g11)
    c: PointOnObject(g19,g10)
    c: Tangent(g11,g18) = -1.5708
    c: Tangent(g10,g18) = -1.5708
    c: PointOnObject(g21,g10)
    c: PointOnObject(g21,g9)
    c: Tangent(g10,g20) = -1.5708
    c: Tangent(g9,g20) = -1.5708
    c: PointOnObject(g23,g9)
    c: PointOnObject(g23,g8)
    c: Tangent(g9,g22) = -1.5708
    c: Tangent(g8,g22) = -1.5708
    c: PointOnObject(g25,g8)
    c: PointOnObject(g25,g7)
    c: Tangent(g8,g24) = -1.5708
    c: Tangent(g7,g24) = -1.5708
    c: Equal(g8,g7)
    c: Equal(g7,g12)
    c: Equal(g12,g11)
    c: Equal(g11,g10)
    c: Equal(g10,g9)
    c: Equal(g18,g20)
    c: Equal(g20,g22)
    c: Equal(g22,g24)
    c: Equal(g24,g14)
    c: Equal(g14,g16)
    c: Distance(g7,g10) = 9  'outer_diam'
    c: Radius(g14) = 1  'outer_fillet'
    c: Vertical(g7)
    c: Vertical(g0)
    c: DistanceX(g0,g3) = 5.55  'nut_max_diam'
    c: Coincident(g26,g1)
    c: Perpendicular(g26,g8) = 1.5708
    c: Distance(g26,g26) = 1.725  'wall_thickness'
FEATURE [PartDesign::AdditiveLoft] AdditiveLoft  label="spc_end_profile"
  Closed = false
  Profile = -> Sketch007
  Refine = true
  Ruled = false
  Sections = -> [Sketch008]
  Suppressed = false
FEATURE [PartDesign::Chamfer] Chamfer006  label="spc_end_chmf"
  Angle = 45
  Base = -> AdditiveLoft [Edge23]
  BaseFeature = -> AdditiveLoft
  ChamferType = 0
  FlipDirection = false
  Refine = true
  Size = 0.4
  Size2 = 1
  SupportTransform = false
  Suppressed = false
  UseAllEdges = false
FEATURE [PartDesign::Chamfer] Chamfer007  label="spc_end_nut_chmf"
  Angle = 45
  Base = -> Chamfer006 [Edge13,Edge18,Edge17,Edge16,Edge15,Edge14]
  BaseFeature = -> Chamfer006
  ChamferType = 0
  FlipDirection = false
  Refine = true
  Size = 0.4
  Size2 = 1
  SupportTransform = false
  Suppressed = false
  UseAllEdges = false
FEATURE [PartDesign::Body] Body003  label="spacer_end"
  AllowCompound = false
  Group = -> [Sketch007,Sketch008,AdditiveLoft,Chamfer006,Chamfer007]
  Origin = -> Origin003
  Tip = -> Chamfer007
FEATURE [PartDesign::FeatureBase] Clone001  label="spc_extr_cln"
  BaseFeature = -> Body003
  Suppressed = false
FEATURE [Sketcher::SketchObject] Sketch009  label="spc_extr_s"
  ArcFitTolerance = 1e-06
  AttachmentSupport = -> [XY_Plane004]
  ExternalTypes = [0]
  FullyConstrained = true
  MakeInternals = false
  MapMode = 5
  _ExternalGeoVersion = 0
  expr: .Constraints.end_length = <<spc_end_base_s>>.Constraints.end_length
  expr: .Constraints.hole_diam = <<spc_end_base_s>>.Constraints.hole_diam
  expr: .Constraints.outer_diam = <<spc_end_base_s>>.Constraints.outer_diam
  expr: .Constraints.outer_fillet = <<spc_end_base_s>>.Constraints.outer_fillet
  sketch-geometry (22):
    g0: Circle CenterX=0 CenterY=0 CenterZ=0 NormalX=0 NormalY=0 NormalZ=1 AngleXU=0 Radius=1.7
    g1: LineSegment StartX=-4.5 StartY=2.02073 StartZ=0 EndX=-4.5 EndY=-2.02073 EndZ=0
    g2: LineSegment StartX=-4 StartY=-2.88675 StartZ=0 EndX=-0.5 EndY=-4.90748 EndZ=0
    g3: LineSegment StartX=0.5 StartY=-4.90748 StartZ=0 EndX=4 EndY=-2.88675 EndZ=0
    g4: LineSegment StartX=4.5 StartY=-2.02073 StartZ=0 EndX=4.5 EndY=2.02073 EndZ=0
    g5: LineSegment StartX=4 StartY=2.88675 StartZ=0 EndX=0.5 EndY=4.90748 EndZ=0
    g6: LineSegment StartX=-0.5 StartY=4.90748 StartZ=0 EndX=-4 EndY=2.88675 EndZ=0
    g7: Circle [constr] CenterX=0 CenterY=0 CenterZ=0 NormalX=0 NormalY=0 NormalZ=1 AngleXU=0 Radius=5.19615
    g8: ArcOfCircle CenterX=-3.5 CenterY=2.02073 CenterZ=0 NormalX=0 NormalY=0 NormalZ=1 AngleXU=0 Radius=1 StartAngle=2.0944 EndAngle=3.14159
    g9: GeomPoint [constr] X=-4.5 Y=2.59808 Z=0
    g10: ArcOfCircle CenterX=2e-16 CenterY=4.04145 CenterZ=0 NormalX=0 NormalY=0 NormalZ=1 AngleXU=0 Radius=1 StartAngle=1.0472 EndAngle=2.0944
    g11: GeomPoint [constr] X=1.4e-15 Y=5.19615 Z=0
    g12: ArcOfCircle CenterX=3.5 CenterY=2.02073 CenterZ=0 NormalX=0 NormalY=0 NormalZ=1 AngleXU=0 Radius=1 StartAngle=0 EndAngle=1.0472
    g13: GeomPoint [constr] X=4.5 Y=2.59808 Z=0
    g14: ArcOfCircle CenterX=3.5 CenterY=-2.02073 CenterZ=0 NormalX=0 NormalY=0 NormalZ=1 AngleXU=0 Radius=1 StartAngle=5.23599 EndAngle=6.28319
    g15: GeomPoint [constr] X=4.5 Y=-2.59808 Z=0
    g16: ArcOfCircle CenterX=1e-16 CenterY=-4.04145 CenterZ=0 NormalX=0 NormalY=0 NormalZ=1 AngleXU=0 Radius=1 StartAngle=4.18879 EndAngle=5.23599
    g17: GeomPoint [constr] X=-1.3e-15 Y=-5.19615 Z=0
    g18: ArcOfCircle CenterX=-3.5 CenterY=-2.02073 CenterZ=0 NormalX=0 NormalY=0 NormalZ=1 AngleXU=0 Radius=1 StartAngle=3.14159 EndAngle=4.18879
    g19: GeomPoint [constr] X=-4.5 Y=-2.59808 Z=0
    g20: LineSegment [constr] StartX=0 StartY=0 StartZ=0 EndX=4.5 EndY=0 EndZ=0
    g21: LineSegment [constr] StartX=4.5 StartY=0 StartZ=0 EndX=13.4 EndY=0 EndZ=0
  constraints (53):
    c: Coincident(g0,g-1)
    c: PointOnObject(g19,g7)
    c: PointOnObject(g17,g7)
    c: PointOnObject(g15,g7)
    c: PointOnObject(g13,g7)
    c: PointOnObject(g11,g7)
    c: PointOnObject(g9,g7)
    c: Coincident(g7,g0)
    c: PointOnObject(g9,g1)
    c: PointOnObject(g9,g6)
    c: Tangent(g1,g8) = -1.5708
    c: Tangent(g6,g8) = -1.5708
    c: PointOnObject(g11,g6)
    c: PointOnObject(g11,g5)
    c: Tangent(g6,g10) = -1.5708
    c: Tangent(g5,g10) = -1.5708
    c: PointOnObject(g13,g5)
    c: PointOnObject(g13,g4)
    c: Tangent(g5,g12) = -1.5708
    c: Tangent(g4,g12) = -1.5708
    c: PointOnObject(g15,g4)
    c: PointOnObject(g15,g3)
    c: Tangent(g4,g14) = -1.5708
    c: Tangent(g3,g14) = -1.5708
    c: PointOnObject(g17,g3)
    c: PointOnObject(g17,g2)
    c: Tangent(g3,g16) = -1.5708
    c: Tangent(g2,g16) = -1.5708
    c: PointOnObject(g19,g2)
    c: PointOnObject(g19,g1)
    c: Tangent(g2,g18) = -1.5708
    c: Tangent(g1,g18) = -1.5708
    c: Equal(g16,g18)
    c: Equal(g18,g8)
    c: Equal(g8,g10)
    c: Equal(g10,g12)
    c: Equal(g12,g14)
    c: Equal(g4,g3)
    c: Equal(g3,g2)
    c: Equal(g2,g1)
    c: Equal(g1,g6)
    c: Equal(g6,g5)
    c: Vertical(g1)
    c: Distance(g1,g4) = 9  'outer_diam'
    c: Radius(g14) = 1  'outer_fillet'
    c: Diameter(g0) = 3.4  'hole_diam'
    c: Coincident(g20,g0)
    c: Coincident(g20,g21)
    c: PointOnObject(g21,g-1)
    c: Distance(g20,g20) = 4.5  'end_length'
    c: DistanceX(g0,g21) = 13.4  'spacer_length'
    c: Distance(g21,g21) = 8.9  'extrude'
    c: PointOnObject(g20,g-1)
FEATURE [PartDesign::Pad] Pad001  label="spc_extr_e"
  BaseFeature = -> Clone001
  Direction = (0,0,1)
  Length = 8.9
  Length2 = 10
  Profile = -> Sketch009
  ReferenceAxis = -> Sketch009 [N_Axis]
  Refine = true
  Reversed = true
  SideType = 0
  Suppressed = false
  Type = 0
  Type2 = 0
  expr: Length = <<spc_extr_s>>.Constraints.extrude
FEATURE [PartDesign::Chamfer] Chamfer008  label="spc_extr_btm_chmf"
  Angle = 45
  Base = -> Pad001 [Edge73]
  BaseFeature = -> Pad001
  ChamferType = 0
  FlipDirection = false
  Refine = true
  Size = 0.4
  Size2 = 1
  SupportTransform = false
  Suppressed = false
  UseAllEdges = false
  expr: Size = <<spc_end_chmf>>.Size
FEATURE [PartDesign::Body] Body004  label="spacer_extrusion"
  AllowCompound = false
  Group = -> [Clone001,Sketch009,Pad001,Chamfer008]
  Origin = -> Origin004
  Tip = -> Chamfer008
FEATURE [PartDesign::FeatureBase] Clone  label="spc_deck_cln"
  BaseFeature = -> Body003
  Suppressed = false
FEATURE [Sketcher::SketchObject] Sketch010  label="spc_deck_s"
  ArcFitTolerance = 1e-06
  AttachmentSupport = -> [XY_Plane005]
  ExternalTypes = [0]
  FullyConstrained = true
  MakeInternals = false
  MapMode = 5
  _ExternalGeoVersion = 0
  expr: .Constraints.end_length = <<spc_end_base_s>>.Constraints.end_length
  expr: .Constraints.extr_spc_length = <<spc_extr_s>>.Constraints.spacer_length
  expr: .Constraints.hole_diam = <<spc_end_base_s>>.Constraints.hole_diam
  expr: .Constraints.outer_diam = <<spc_end_base_s>>.Constraints.outer_diam
  expr: .Constraints.outer_fillet = <<spc_end_base_s>>.Constraints.outer_fillet
  sketch-geometry (23):
    g0: LineSegment StartX=-4.5 StartY=2.02073 StartZ=0 EndX=-4.5 EndY=-2.02073 EndZ=0
    g1: LineSegment StartX=-4 StartY=-2.88675 StartZ=0 EndX=-0.5 EndY=-4.90748 EndZ=0
    g2: LineSegment StartX=0.5 StartY=-4.90748 StartZ=0 EndX=4 EndY=-2.88675 EndZ=0
    g3: LineSegment StartX=4.5 StartY=-2.02073 StartZ=0 EndX=4.5 EndY=2.02073 EndZ=0
    g4: LineSegment StartX=4 StartY=2.88675 StartZ=0 EndX=0.5 EndY=4.90748 EndZ=0
    g5: LineSegment StartX=-0.5 StartY=4.90748 StartZ=0 EndX=-4 EndY=2.88675 EndZ=0
    g6: Circle [constr] CenterX=0 CenterY=0 CenterZ=0 NormalX=0 NormalY=0 NormalZ=1 AngleXU=0 Radius=5.19615
    g7: Circle CenterX=0 CenterY=0 CenterZ=0 NormalX=0 NormalY=0 NormalZ=1 AngleXU=0 Radius=1.7
    g8: GeomPoint [constr] X=4.5 Y=0 Z=0
    g9: GeomPoint [constr] X=13.4 Y=0 Z=0
    g10: GeomPoint [constr] X=33.4 Y=0 Z=0
    g11: ArcOfCircle CenterX=6e-16 CenterY=4.04145 CenterZ=0 NormalX=0 NormalY=0 NormalZ=1 AngleXU=0 Radius=1 StartAngle=1.0472 EndAngle=2.0944
    g12: GeomPoint [constr] X=6e-16 Y=5.19615 Z=0
    g13: ArcOfCircle CenterX=3.5 CenterY=2.02073 CenterZ=0 NormalX=0 NormalY=0 NormalZ=1 AngleXU=0 Radius=1 StartAngle=0 EndAngle=1.0472
    g14: GeomPoint [constr] X=4.5 Y=2.59808 Z=0
    g15: ArcOfCircle CenterX=3.5 CenterY=-2.02073 CenterZ=0 NormalX=0 NormalY=0 NormalZ=1 AngleXU=0 Radius=1 StartAngle=5.23599 EndAngle=6.28319
    g16: GeomPoint [constr] X=4.5 Y=-2.59808 Z=0
    g17: ArcOfCircle CenterX=3e-16 CenterY=-4.04145 CenterZ=0 NormalX=0 NormalY=0 NormalZ=1 AngleXU=0 Radius=1 StartAngle=4.18879 EndAngle=5.23599
    g18: GeomPoint [constr] X=2.4e-15 Y=-5.19615 Z=0
    g19: ArcOfCircle CenterX=-3.5 CenterY=-2.02073 CenterZ=0 NormalX=0 NormalY=0 NormalZ=1 AngleXU=0 Radius=1 StartAngle=3.14159 EndAngle=4.18879
    g20: GeomPoint [constr] X=-4.5 Y=-2.59808 Z=0
    g21: ArcOfCircle CenterX=-3.5 CenterY=2.02073 CenterZ=0 NormalX=0 NormalY=0 NormalZ=1 AngleXU=0 Radius=1 StartAngle=2.0944 EndAngle=3.14159
    g22: GeomPoint [constr] X=-4.5 Y=2.59808 Z=0
  constraints (54):
    c: PointOnObject(g20,g6)
    c: PointOnObject(g18,g6)
    c: PointOnObject(g16,g6)
    c: PointOnObject(g14,g6)
    c: PointOnObject(g12,g6)
    c: PointOnObject(g22,g6)
    c: Coincident(g6,g-1)
    c: Coincident(g7,g6)
    c: PointOnObject(g8,g-1)
    c: PointOnObject(g9,g-1)
    c: PointOnObject(g10,g-1)
    c: PointOnObject(g12,g5)
    c: PointOnObject(g12,g4)
    c: Tangent(g5,g11) = -1.5708
    c: Tangent(g4,g11) = -1.5708
    c: PointOnObject(g14,g4)
    c: PointOnObject(g14,g3)
    c: Tangent(g4,g13) = -1.5708
    c: Tangent(g3,g13) = -1.5708
    c: PointOnObject(g16,g3)
    c: PointOnObject(g16,g2)
    c: Tangent(g3,g15) = -1.5708
    c: Tangent(g2,g15) = -1.5708
    c: PointOnObject(g18,g2)
    c: PointOnObject(g18,g1)
    c: Tangent(g2,g17) = -1.5708
    c: Tangent(g1,g17) = -1.5708
    c: PointOnObject(g20,g1)
    c: PointOnObject(g20,g0)
    c: Tangent(g1,g19) = -1.5708
    c: Tangent(g0,g19) = -1.5708
    c: PointOnObject(g22,g0)
    c: PointOnObject(g22,g5)
    c: Tangent(g0,g21) = -1.5708
    c: Tangent(g5,g21) = -1.5708
    c: Equal(g3,g2)
    c: Equal(g2,g1)
    c: Equal(g1,g0)
    c: Equal(g0,g5)
    c: Equal(g5,g4)
    c: Equal(g13,g15)
    c: Equal(g15,g17)
    c: Equal(g17,g19)
    c: Equal(g19,g21)
    c: Equal(g21,g11)
    c: Vertical(g0)
    c: Distance(g0,g3) = 9  'outer_diam'
    c: Radius(g17) = 1  'outer_fillet'
    c: Diameter(g7) = 3.4  'hole_diam'
    c: Distance(g6,g8) = 4.5  'end_length'
    c: Distance(g6,g9) = 13.4  'extr_spc_length'
    c: DistanceX(g9,g10) = 20  'deck_diff'
    c: DistanceX(g8,g10) = 28.9  'extrude'
    c: Distance(g6,g10) = 33.4  'spacer_length'
FEATURE [PartDesign::Pad] Pad002  label="spc_deck_e"
  BaseFeature = -> Clone
  Direction = (0,0,1)
  Length = 28.9
  Length2 = 10
  Profile = -> Sketch010
  ReferenceAxis = -> Sketch010 [N_Axis]
  Refine = true
  Reversed = true
  SideType = 0
  Suppressed = false
  Type = 0
  Type2 = 0
  expr: Length = <<spc_deck_s>>.Constraints.extrude
FEATURE [PartDesign::Chamfer] Chamfer009  label="spc_deck_btm_chmf"
  Angle = 45
  Base = -> Pad002 [Edge73]
  BaseFeature = -> Pad002
  ChamferType = 0
  FlipDirection = false
  Refine = true
  Size = 0.4
  Size2 = 1
  SupportTransform = false
  Suppressed = false
  UseAllEdges = false
  expr: Size = <<spc_end_chmf>>.Size
FEATURE [PartDesign::Body] Body005  label="spacer_deck"
  AllowCompound = false
  Group = -> [Clone,Sketch010,Pad002,Chamfer009]
  Origin = -> Origin005
  Tip = -> Chamfer009
FEATURE [PartDesign::FeatureBase] Clone002  label="spc_foot_cln"
  BaseFeature = -> Body003
  Suppressed = false
FEATURE [Sketcher::SketchObject] Sketch011  label="spc_foot_s"
  ArcFitTolerance = 1e-06
  AttachmentSupport = -> [XY_Plane006]
  ExternalTypes = [0]
  FullyConstrained = true
  MakeInternals = false
  MapMode = 5
  _ExternalGeoVersion = 0
  expr: .Constraints.end_length = <<spc_end_base_s>>.Constraints.end_length
  expr: .Constraints.hole_diam = <<spc_end_base_s>>.Constraints.hole_diam
  expr: .Constraints.outer_diam = <<spc_end_base_s>>.Constraints.outer_diam
  expr: .Constraints.outer_fillet = <<spc_end_base_s>>.Constraints.outer_fillet
  sketch-geometry (22):
    g0: GeomPoint [constr] X=4.5 Y=0 Z=0
    g1: GeomPoint [constr] X=10 Y=0 Z=0
    g2: LineSegment StartX=-4.5 StartY=2.02073 StartZ=0 EndX=-4.5 EndY=-2.02073 EndZ=0
    g3: LineSegment StartX=-4 StartY=-2.88675 StartZ=0 EndX=-0.5 EndY=-4.90748 EndZ=0
    g4: LineSegment StartX=0.5 StartY=-4.90748 StartZ=0 EndX=4 EndY=-2.88675 EndZ=0
    g5: LineSegment StartX=4.5 StartY=-2.02073 StartZ=0 EndX=4.5 EndY=2.02073 EndZ=0
    g6: LineSegment StartX=4 StartY=2.88675 StartZ=0 EndX=0.5 EndY=4.90748 EndZ=0
    g7: LineSegment StartX=-0.5 StartY=4.90748 StartZ=0 EndX=-4 EndY=2.88675 EndZ=0
    g8: Circle [constr] CenterX=0 CenterY=0 CenterZ=0 NormalX=0 NormalY=0 NormalZ=1 AngleXU=0 Radius=5.19615
    g9: Circle CenterX=0 CenterY=0 CenterZ=0 NormalX=0 NormalY=0 NormalZ=1 AngleXU=0 Radius=1.7
    g10: ArcOfCircle CenterX=-3.5 CenterY=2.02073 CenterZ=0 NormalX=0 NormalY=0 NormalZ=1 AngleXU=0 Radius=1 StartAngle=2.0944 EndAngle=3.14159
    g11: GeomPoint [constr] X=-4.5 Y=2.59808 Z=0
    g12: ArcOfCircle CenterX=-8e-16 CenterY=4.04145 CenterZ=0 NormalX=0 NormalY=0 NormalZ=1 AngleXU=0 Radius=1 StartAngle=1.0472 EndAngle=2.0944
    g13: GeomPoint [constr] X=7e-16 Y=5.19615 Z=0
    g14: ArcOfCircle CenterX=3.5 CenterY=2.02073 CenterZ=0 NormalX=0 NormalY=0 NormalZ=1 AngleXU=0 Radius=1 StartAngle=0 EndAngle=1.0472
    g15: GeomPoint [constr] X=4.5 Y=2.59808 Z=0
    g16: ArcOfCircle CenterX=3.5 CenterY=-2.02073 CenterZ=0 NormalX=0 NormalY=0 NormalZ=1 AngleXU=0 Radius=1 StartAngle=5.23599 EndAngle=6.28319
    g17: GeomPoint [constr] X=4.5 Y=-2.59808 Z=0
    g18: ArcOfCircle CenterX=5e-16 CenterY=-4.04145 CenterZ=0 NormalX=0 NormalY=0 NormalZ=1 AngleXU=0 Radius=1 StartAngle=4.18879 EndAngle=5.23599
    g19: GeomPoint [constr] X=1e-16 Y=-5.19615 Z=0
    g20: ArcOfCircle CenterX=-3.5 CenterY=-2.02073 CenterZ=0 NormalX=0 NormalY=0 NormalZ=1 AngleXU=0 Radius=1 StartAngle=3.14159 EndAngle=4.18879
    g21: GeomPoint [constr] X=-4.5 Y=-2.59808 Z=0
  constraints (51):
    c: PointOnObject(g0,g-1)
    c: PointOnObject(g1,g-1)
    c: PointOnObject(g21,g8)
    c: PointOnObject(g19,g8)
    c: PointOnObject(g17,g8)
    c: PointOnObject(g15,g8)
    c: PointOnObject(g13,g8)
    c: PointOnObject(g11,g8)
    c: Coincident(g8,g-1)
    c: Coincident(g9,g8)
    c: PointOnObject(g11,g2)
    c: PointOnObject(g11,g7)
    c: Tangent(g2,g10) = -1.5708
    c: Tangent(g7,g10) = -1.5708
    c: PointOnObject(g13,g7)
    c: PointOnObject(g13,g6)
    c: Tangent(g7,g12) = -1.5708
    c: Tangent(g6,g12) = -1.5708
    c: PointOnObject(g15,g6)
    c: PointOnObject(g15,g5)
    c: Tangent(g6,g14) = -1.5708
    c: Tangent(g5,g14) = -1.5708
    c: PointOnObject(g17,g5)
    c: PointOnObject(g17,g4)
    c: Tangent(g5,g16) = -1.5708
    c: Tangent(g4,g16) = -1.5708
    c: PointOnObject(g19,g4)
    c: PointOnObject(g19,g3)
    c: Tangent(g4,g18) = -1.5708
    c: Tangent(g3,g18) = -1.5708
    c: PointOnObject(g21,g3)
    c: PointOnObject(g21,g2)
    c: Tangent(g3,g20) = -1.5708
    c: Tangent(g2,g20) = -1.5708
    c: Equal(g3,g2)
    c: Equal(g2,g7)
    c: Equal(g7,g6)
    c: Equal(g6,g5)
    c: Equal(g5,g4)
    c: Equal(g16,g18)
    c: Equal(g18,g20)
    c: Equal(g20,g10)
    c: Equal(g10,g12)
    c: Equal(g12,g14)
    c: Vertical(g2)
    c: Distance(g2,g5) = 9  'outer_diam'
    c: Radius(g18) = 1  'outer_fillet'
    c: Diameter(g9) = 3.4  'hole_diam'
    c: DistanceX(g8,g0) = 4.5  'end_length'
    c: DistanceX(g0,g1) = 5.5  'extrude'
    c: DistanceX(g8,g1) = 10  'spacer_length'
FEATURE [PartDesign::Pad] Pad003  label="spc_foot_e"
  BaseFeature = -> Clone002
  Direction = (0,0,1)
  Length = 5.5
  Length2 = 10
  Profile = -> Sketch011
  ReferenceAxis = -> Sketch011 [N_Axis]
  Refine = true
  Reversed = true
  SideType = 0
  Suppressed = false
  Type = 0
  Type2 = 0
  expr: Length = <<spc_foot_s>>.Constraints.extrude
FEATURE [PartDesign::Chamfer] Chamfer010  label="spc_foot_btm_chmf"
  Angle = 45
  Base = -> Pad003 [Edge73]
  BaseFeature = -> Pad003
  ChamferType = 0
  FlipDirection = false
  Refine = true
  Size = 0.4
  Size2 = 1
  SupportTransform = false
  Suppressed = false
  UseAllEdges = false
  expr: Size = <<spc_end_chmf>>.Size
FEATURE [Sketcher::SketchObject] Sketch012  label="spc_foot_head_pckt_s"
  ArcFitTolerance = 1e-06
  AttachmentOffset = pos=(0,0,4.5) rot=(0,0,1;0rad)
  AttachmentSupport = -> [XY_Plane006]
  ExternalTypes = [0]
  FullyConstrained = true
  MakeInternals = false
  MapMode = 5
  Placement = pos=(0,0,4.5) rot=(0,0,1;0rad)
  _ExternalGeoVersion = 0
  expr: .AttachmentOffset.Base.z = <<spc_end_base_s>>.Constraints.end_length
  sketch-geometry (1):
    g0: Circle CenterX=0 CenterY=0 CenterZ=0 NormalX=0 NormalY=0 NormalZ=1 AngleXU=0 Radius=2.925
  constraints (2):
    c: Coincident(g0,g-1)
    c: Diameter(g0) = 5.85  'head_diam'
FEATURE [PartDesign::Pocket] Pocket002  label="spc_foot_head_pocket"
  BaseFeature = -> Chamfer010
  Direction = (0,0,-1)
  Length = 4.5
  Length2 = 5
  Profile = -> Sketch012
  ReferenceAxis = -> Sketch012 [N_Axis]
  Refine = true
  SideType = 0
  Suppressed = false
  Type = 0
  Type2 = 0
  expr: Length = <<spc_end_base_s>>.Constraints.end_length
FEATURE [PartDesign::Body] Body006  label="spacer_foot"
  AllowCompound = false
  Group = -> [Clone002,Sketch011,Pad003,Chamfer010,Sketch012,Pocket002]
  Origin = -> Origin006
  Tip = -> Pocket002
FEATURE [App::Point] Origin007  label="Origin"
  Role = Origin
FEATURE [App::Point] Origin008  label="Origin"
  Role = Origin
FEATURE [App::Point] Origin009  label="Origin"
  Role = Origin
FEATURE [App::Point] Origin010  label="Origin"
  Role = Origin
FEATURE [App::Point] Origin011  label="Origin"
  Role = Origin
